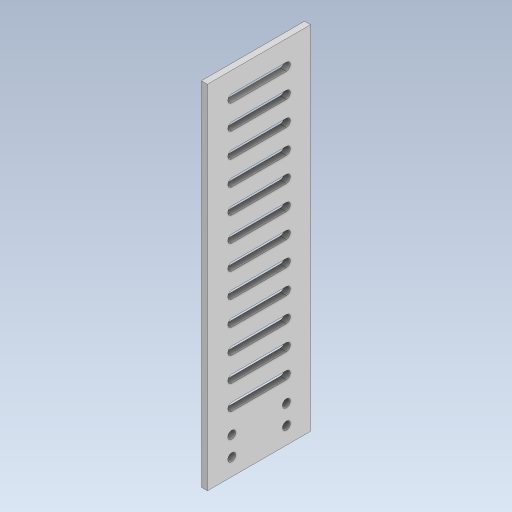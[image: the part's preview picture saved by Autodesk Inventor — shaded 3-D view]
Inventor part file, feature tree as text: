
AUTODESK INVENTOR PART (.ipt)
format: ipt  version: 2023.5 (Build 275446000, 446)  size: 196,608 bytes
history: native  units: mm
features: extrude x1, sketch x1
ambient origin geometry x8: Origin, YZ Plane, XZ Plane, XY Plane, X Axis, Y Axis, Z Axis, Center Point
bodies: Solid1 (feature_tree)
feature tree (2):
  extrude  "Extrusion1"  Depth=3.3mm
  sketch  "Sketch1"  dims[d1=3.3mm d3=3.3mm d5=3.3mm d6=10.0mm d7=10.0mm d9=3.3mm d11=120.0mm d13=10.0mm d14=10.0mm d16=10.0mm d18=2.5mm d19=0.0mm d20=15.0mm d22=7.0mm d23=7.0mm d24=8.0mm d25=3.3mm d26=8.0mm d27=8.0mm]
